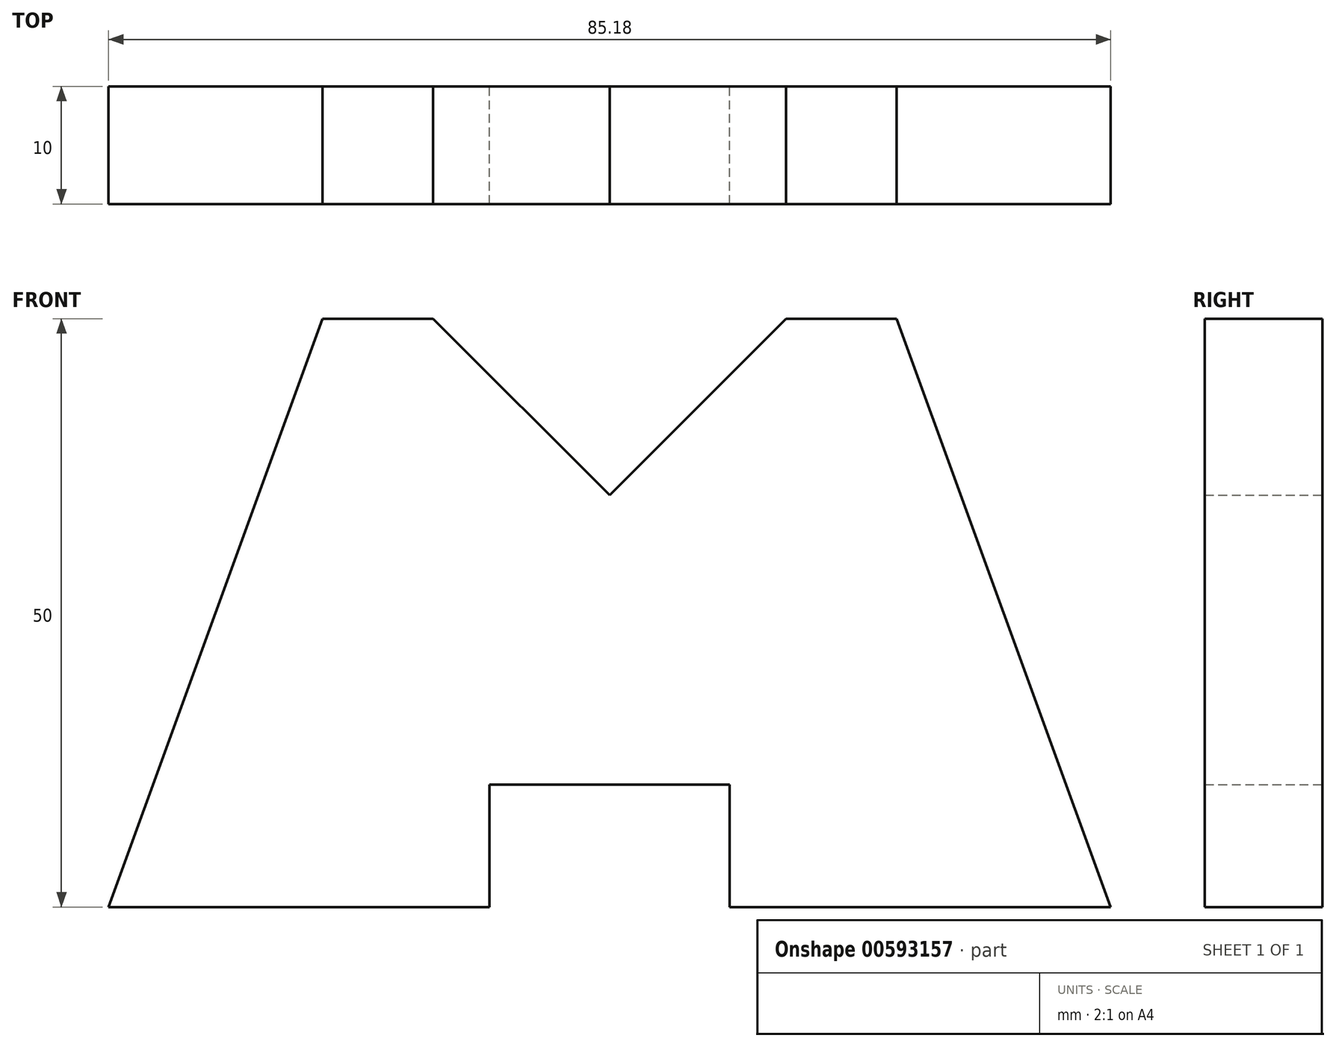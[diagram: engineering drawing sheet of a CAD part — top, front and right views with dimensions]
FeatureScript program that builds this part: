
annotation { "Feature Type Name" : "Feature", "Feature Type Description" : "" }
export const myFeature = defineFeature(function(context is Context, id is Id, definition is map)
    precondition{}
    {
        {
            var Q0;
            Q0=qCreatedBy(makeId("Front.planeOp"),FACE);
            var sketch = newSketch(context, id + "F0", { "sketchPlane" : qUnion([Q0])});
            skLineSegment(sketch, "E0", {"start": v(5.6, 50) * mm, "end": v(15, 50) * mm});
            skLineSegment(sketch, "E1", {"start": v(15, 50) * mm, "end": v(30, 35) * mm});
            skLineSegment(sketch, "E2", {"start": v(30, 35) * mm, "end": v(45, 50) * mm});
            skLineSegment(sketch, "E3", {"start": v(45, 50) * mm, "end": v(54.4, 50) * mm});
            skLineSegment(sketch, "E4", {"start": v(72.6, 0) * mm, "end": v(40.2, 0) * mm});
            skLineSegment(sketch, "E5", {"start": v(40.2, 0) * mm, "end": v(40.2, 10.4) * mm});
            skLineSegment(sketch, "E6", {"start": v(40.2, 10.4) * mm, "end": v(19.8, 10.4) * mm});
            skLineSegment(sketch, "E7", {"start": v(19.8, 10.4) * mm, "end": v(19.8, 0) * mm});
            skLineSegment(sketch, "E8", {"start": v(5.6, 50) * mm, "end": v(-12.6, 0) * mm});
            skLineSegment(sketch, "E9", {"start": v(54.4, 50) * mm, "end": v(72.6, 0) * mm});
            skLineSegment(sketch, "E10", {"start": v(-12.6, 0) * mm, "end": v(19.8, 0) * mm});
            skLineSegment(sketch, "E11", {"start": v(30, 35) * mm, "end": v(30, 10.4) * mm, "construction": true});
            skSolve(sketch);
        }
        {
            var Q0;
            Q0=makeQuery(id+"F0.imprint","IMPRINT",FACE,{"disambiguationData":[TD([[makeQuery(id+"F0.imprint","IMPRINT",EDGE,{"derivedFrom":sQuery(id+"F0.wireOp",EDGE,"yGOMhLO9-tLpQ-TU6H-iEPR-mg8r4xAotPJb")}),-1.0]])]});
            var Q1;
            Q1=makeQuery(id+"F0.imprint","IMPRINT",FACE,{"disambiguationData":[TD([[makeQuery(id+"F0.imprint","IMPRINT",EDGE,{"derivedFrom":sQuery(id+"F0.wireOp",EDGE,"E0")}),-1.0]])]});
            extrude(context, id + "F1", {"entities" : qUnion([Q0, Q1]), "depth" : 10 * mm, "offsetDistance" : 25.4 * mm});
        }
    });
